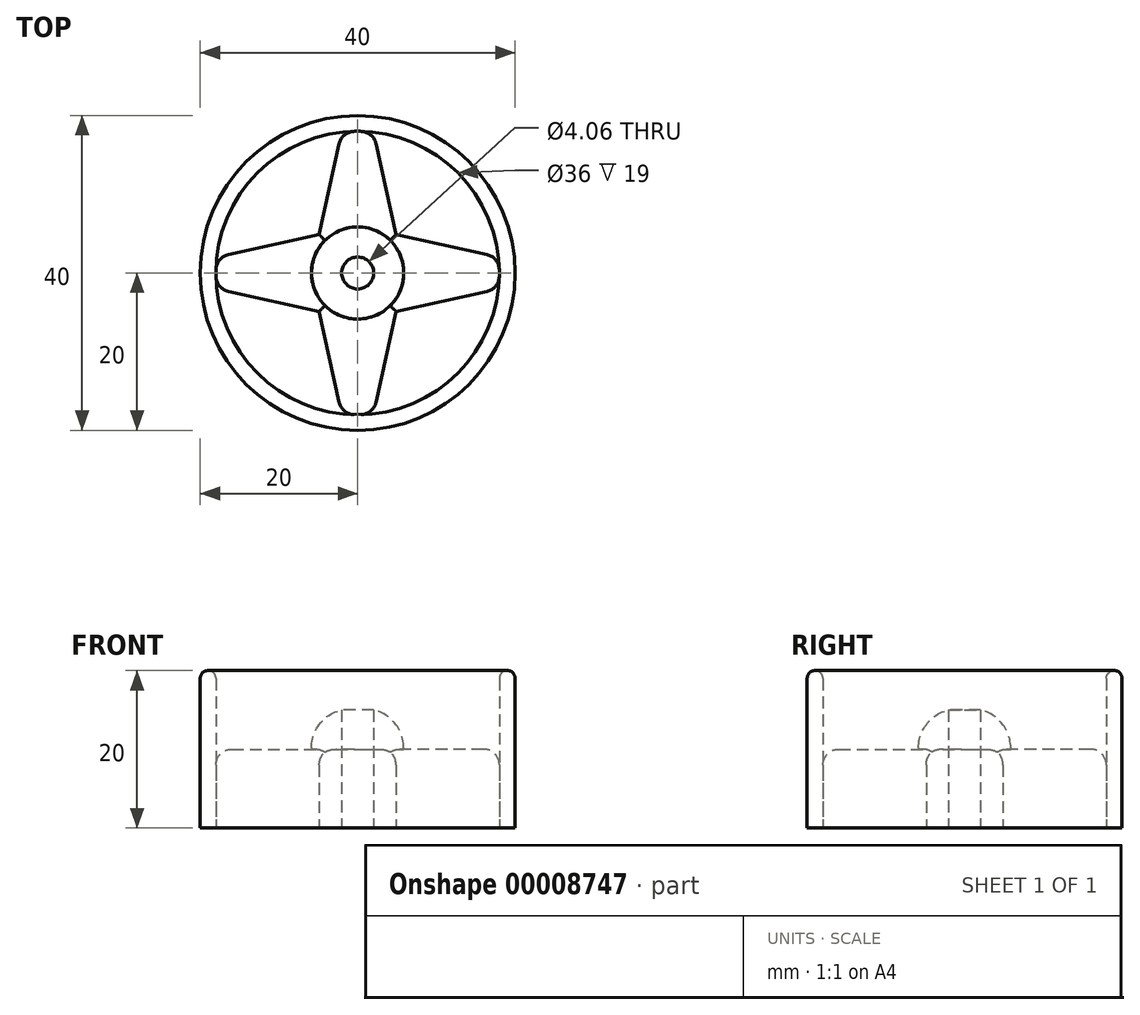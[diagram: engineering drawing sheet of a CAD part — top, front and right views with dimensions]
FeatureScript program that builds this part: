
annotation { "Feature Type Name" : "Feature", "Feature Type Description" : "" }
export const myFeature = defineFeature(function(context is Context, id is Id, definition is map)
    precondition{}
    {
        {
            var Q0;
            Q0=qCreatedBy(makeId("Top.planeOp"),FACE);
            var sketch = newSketch(context, id + "F0", { "sketchPlane" : qUnion([Q0])});
            skCircle(sketch, "E0", {"center": v(0, 0) * mm, "radius": 20 * mm});
            skCircle(sketch, "E1.0", {"center": v(0, 0) * mm, "radius": 18 * mm});
            skCircle(sketch, "E2", {"center": v(0, 0) * mm, "radius": 5.86 * mm});
            skCircle(sketch, "E3", {"center": v(0, 0) * mm, "radius": 2.03 * mm});
            skLineSegment(sketch, "E4", {"start": v(-2.03, 17.89) * mm, "end": v(-4.88, 4.88) * mm});
            skLineSegment(sketch, "E5", {"start": v(-17.89, 2.03) * mm, "end": v(-4.88, 4.88) * mm});
            skLineSegment(sketch, "E6.0.MirrorCS", {"start": v(-17.89, -2.03) * mm, "end": v(-4.88, -4.88) * mm});
            skLineSegment(sketch, "E7.0.MirrorCS", {"start": v(17.89, 2.03) * mm, "end": v(4.88, 4.88) * mm});
            skLineSegment(sketch, "E8.0.MirrorCS", {"start": v(17.89, -2.03) * mm, "end": v(4.88, -4.88) * mm});
            skLineSegment(sketch, "E9.0.MirrorCS", {"start": v(2.03, 17.89) * mm, "end": v(4.88, 4.88) * mm});
            skLineSegment(sketch, "E10.0.MirrorCS", {"start": v(-2.03, -17.89) * mm, "end": v(-4.88, -4.88) * mm});
            skLineSegment(sketch, "E11.0.MirrorCS", {"start": v(2.03, -17.89) * mm, "end": v(4.88, -4.88) * mm});
            skPoint(sketch, "E12.start.orphan", {"position": v(0, 18) * mm});
            skPoint(sketch, "E13.orphan", {"position": v(-2, 5.5) * mm});
            skPoint(sketch, "E14.orphan", {"position": v(-5.5, 2) * mm});
            skPoint(sketch, "E15.start.orphan", {"position": v(-5.86, 0) * mm});
            skSolve(sketch);
        }
        {
            var Q0;
            Q0=makeQuery(id+"F0.imprint","IMPRINT",FACE,{"disambiguationData":[TD([[makeQuery(id+"F0.imprint","IMPRINT",EDGE,{"derivedFrom":sQuery(id+"F0.wireOp",EDGE,"E0")}),1.0]])]});
            extrude(context, id + "F1", {"entities" : qUnion([Q0]), "depth" : 20 * mm});
        }
        {
            var Q0;
            Q0=makeQuery(id+"F0.imprint","IMPRINT",FACE,{"disambiguationData":[TD([[makeQuery(id+"F0.imprint","IMPRINT",EDGE,{"derivedFrom":sQuery(id+"F0.wireOp",EDGE,"E2")}),-1.0]])]});
            extrude(context, id + "F2", {"entities" : qUnion([Q0]), "depth" : 10 * mm});
        }
        {
            var Q0;
            Q0=makeQuery(id+"F0.imprint","IMPRINT",FACE,{"disambiguationData":[TD([[makeQuery(id+"F0.imprint","IMPRINT",EDGE,{"derivedFrom":sQuery(id+"F0.wireOp",EDGE,"E2")}),1.0]])]});
            extrude(context, id + "F3", {"entities" : qUnion([Q0]), "operationType" : NewBodyOperationType.ADD, "depth" : 15 * mm});
        }
        {
            var Q0;
            Q0=makeQuery(id+"F2.opExtrude","CAP_EDGE",EDGE,{"disambiguationData":[OSD([sQuery(id+"F0.wireOp",EDGE,"E4")])],"isStart":false});
            var Q1;
            Q1=makeQuery(id+"F2.opExtrude","CAP_EDGE",EDGE,{"disambiguationData":[OSD([sQuery(id+"F0.wireOp",EDGE,"E5")])],"isStart":false});
            var Q2;
            Q2=makeQuery(id+"F2.opExtrude","CAP_EDGE",EDGE,{"disambiguationData":[OSD([sQuery(id+"F0.wireOp",EDGE,"E6.0.MirrorCS")])],"isStart":false});
            var Q3;
            Q3=makeQuery(id+"F2.opExtrude","CAP_EDGE",EDGE,{"disambiguationData":[OSD([sQuery(id+"F0.wireOp",EDGE,"E10.0.MirrorCS")])],"isStart":false});
            var Q4;
            Q4=makeQuery(id+"F2.opExtrude","CAP_EDGE",EDGE,{"disambiguationData":[OSD([sQuery(id+"F0.wireOp",EDGE,"E11.0.MirrorCS")])],"isStart":false});
            var Q5;
            Q5=makeQuery(id+"F2.opExtrude","CAP_EDGE",EDGE,{"disambiguationData":[OSD([sQuery(id+"F0.wireOp",EDGE,"E8.0.MirrorCS")])],"isStart":false});
            var Q6;
            Q6=makeQuery(id+"F2.opExtrude","CAP_EDGE",EDGE,{"disambiguationData":[OSD([sQuery(id+"F0.wireOp",EDGE,"E7.0.MirrorCS")])],"isStart":false});
            var Q7;
            Q7=makeQuery(id+"F2.opExtrude","CAP_EDGE",EDGE,{"disambiguationData":[OSD([sQuery(id+"F0.wireOp",EDGE,"E9.0.MirrorCS")])],"isStart":false});
            fillet(context, id + "F4", {"entities" : qUnion([Q0, Q1, Q2, Q3, Q4, Q5, Q6, Q7]), "radius" : 2 * mm, "allowEdgeOverflow" : false});
        }
        {
            var Q0;
            Q0=makeQuery(id+"F3.opExtrude","CAP_EDGE",EDGE,{"disambiguationData":[OSD([sQuery(id+"F0.wireOp",EDGE,"E2")])],"isStart":false});
            fillet(context, id + "F5", {"entities" : qUnion([Q0]), "radius" : 5 * mm, "tangentPropagation" : true, "allowEdgeOverflow" : false});
        }
        {
            var Q0;
            Q0=makeQuery(id+"F1.opExtrude","CAP_FACE",FACE,{"disambiguationData":[OSD([sQuery(id+"F0.wireOp",EDGE,"E0"),sQuery(id+"F0.wireOp",EDGE,"E1.0"),sQuery(id+"F0.wireOp",EDGE,"aa337d1e-bd78-4951-a328-375c114ad06f.0"),sQuery(id+"F0.wireOp",EDGE,"7219519c-3e05-4d61-9cbf-932767d396e7.0"),sQuery(id+"F0.wireOp",EDGE,"E4"),sQuery(id+"F0.wireOp",EDGE,"E5")])],"isStart":false});
            fillet(context, id + "F6", {"entities" : qUnion([Q0]), "radius" : 1 * mm, "allowEdgeOverflow" : false});
        }
        {
            var Q0;
            Q0=makeQuery(id+"F4.opFillet","BLEND_EDGE",EDGE,{"blendedFrom":[makeQuery(id+"F2.opExtrude","CAP_EDGE",EDGE,{"disambiguationData":[OSD([sQuery(id+"F0.wireOp",EDGE,"E11.0.MirrorCS")])],"isStart":false}),makeQuery(id+"F1.opExtrude","SWEPT_FACE",FACE,{"disambiguationData":[OSD([sQuery(id+"F0.wireOp",EDGE,"E1.0")])]})],"blendedInto":[makeQuery(id+"F1.opExtrude","SWEPT_FACE",FACE,{"disambiguationData":[OSD([sQuery(id+"F0.wireOp",EDGE,"E1.0")])]})]});
            var Q1;
            Q1=makeQuery(id+"F4.opFillet","BLEND_EDGE",EDGE,{"blendedFrom":[makeQuery(id+"F2.opExtrude","CAP_EDGE",EDGE,{"disambiguationData":[OSD([sQuery(id+"F0.wireOp",EDGE,"E10.0.MirrorCS")])],"isStart":false}),makeQuery(id+"F1.opExtrude","SWEPT_FACE",FACE,{"disambiguationData":[OSD([sQuery(id+"F0.wireOp",EDGE,"E1.0")])]})],"blendedInto":[makeQuery(id+"F1.opExtrude","SWEPT_FACE",FACE,{"disambiguationData":[OSD([sQuery(id+"F0.wireOp",EDGE,"E1.0")])]})]});
            var Q2;
            Q2=makeQuery(id+"F2.opExtrude","SWEPT_EDGE",EDGE,{"disambiguationData":[OSD([sQuery(id+"F0.wireOp",EDGE,"E1.0"),sQuery(id+"F0.wireOp",EDGE,"E11.0.MirrorCS")])]});
            var Q3;
            Q3=makeQuery(id+"F2.opExtrude","SWEPT_EDGE",EDGE,{"disambiguationData":[OSD([sQuery(id+"F0.wireOp",EDGE,"E1.0"),sQuery(id+"F0.wireOp",EDGE,"E10.0.MirrorCS")])]});
            fillet(context, id + "F7", {"entities" : qUnion([Q0, Q1, Q2, Q3]), "radius" : 2 * mm, "tangentPropagation" : true, "allowEdgeOverflow" : false});
        }
        {
            var Q0;
            Q0=makeQuery(id+"F2.opExtrude","SWEPT_EDGE",EDGE,{"disambiguationData":[OSD([sQuery(id+"F0.wireOp",EDGE,"E1.0"),sQuery(id+"F0.wireOp",EDGE,"E8.0.MirrorCS")])]});
            var Q1;
            Q1=makeQuery(id+"F4.opFillet","BLEND_EDGE",EDGE,{"blendedFrom":[makeQuery(id+"F2.opExtrude","CAP_EDGE",EDGE,{"disambiguationData":[OSD([sQuery(id+"F0.wireOp",EDGE,"E8.0.MirrorCS")])],"isStart":false}),makeQuery(id+"F1.opExtrude","SWEPT_FACE",FACE,{"disambiguationData":[OSD([sQuery(id+"F0.wireOp",EDGE,"E1.0")])]})],"blendedInto":[makeQuery(id+"F1.opExtrude","SWEPT_FACE",FACE,{"disambiguationData":[OSD([sQuery(id+"F0.wireOp",EDGE,"E1.0")])]})]});
            var Q2;
            Q2=makeQuery(id+"F4.opFillet","BLEND_EDGE",EDGE,{"blendedFrom":[makeQuery(id+"F2.opExtrude","CAP_EDGE",EDGE,{"disambiguationData":[OSD([sQuery(id+"F0.wireOp",EDGE,"E7.0.MirrorCS")])],"isStart":false}),makeQuery(id+"F1.opExtrude","SWEPT_FACE",FACE,{"disambiguationData":[OSD([sQuery(id+"F0.wireOp",EDGE,"E1.0")])]})],"blendedInto":[makeQuery(id+"F1.opExtrude","SWEPT_FACE",FACE,{"disambiguationData":[OSD([sQuery(id+"F0.wireOp",EDGE,"E1.0")])]})]});
            var Q3;
            Q3=makeQuery(id+"F2.opExtrude","SWEPT_EDGE",EDGE,{"disambiguationData":[OSD([sQuery(id+"F0.wireOp",EDGE,"E1.0"),sQuery(id+"F0.wireOp",EDGE,"E7.0.MirrorCS")])]});
            var Q4;
            Q4=makeQuery(id+"F2.opExtrude","SWEPT_EDGE",EDGE,{"disambiguationData":[OSD([sQuery(id+"F0.wireOp",EDGE,"E1.0"),sQuery(id+"F0.wireOp",EDGE,"E6.0.MirrorCS")])]});
            var Q5;
            Q5=makeQuery(id+"F4.opFillet","BLEND_EDGE",EDGE,{"blendedFrom":[makeQuery(id+"F2.opExtrude","CAP_EDGE",EDGE,{"disambiguationData":[OSD([sQuery(id+"F0.wireOp",EDGE,"E6.0.MirrorCS")])],"isStart":false}),makeQuery(id+"F1.opExtrude","SWEPT_FACE",FACE,{"disambiguationData":[OSD([sQuery(id+"F0.wireOp",EDGE,"E1.0")])]})],"blendedInto":[makeQuery(id+"F1.opExtrude","SWEPT_FACE",FACE,{"disambiguationData":[OSD([sQuery(id+"F0.wireOp",EDGE,"E1.0")])]})]});
            var Q6;
            Q6=makeQuery(id+"F4.opFillet","BLEND_EDGE",EDGE,{"blendedFrom":[makeQuery(id+"F2.opExtrude","CAP_EDGE",EDGE,{"disambiguationData":[OSD([sQuery(id+"F0.wireOp",EDGE,"E5")])],"isStart":false}),makeQuery(id+"F1.opExtrude","SWEPT_FACE",FACE,{"disambiguationData":[OSD([sQuery(id+"F0.wireOp",EDGE,"E1.0")])]})],"blendedInto":[makeQuery(id+"F1.opExtrude","SWEPT_FACE",FACE,{"disambiguationData":[OSD([sQuery(id+"F0.wireOp",EDGE,"E1.0")])]})]});
            var Q7;
            Q7=makeQuery(id+"F2.opExtrude","SWEPT_EDGE",EDGE,{"disambiguationData":[OSD([sQuery(id+"F0.wireOp",EDGE,"E1.0"),sQuery(id+"F0.wireOp",EDGE,"E5")])]});
            var Q8;
            Q8=makeQuery(id+"F2.opExtrude","SWEPT_EDGE",EDGE,{"disambiguationData":[OSD([sQuery(id+"F0.wireOp",EDGE,"E1.0"),sQuery(id+"F0.wireOp",EDGE,"E4")])]});
            var Q9;
            Q9=makeQuery(id+"F4.opFillet","BLEND_EDGE",EDGE,{"blendedFrom":[makeQuery(id+"F2.opExtrude","CAP_EDGE",EDGE,{"disambiguationData":[OSD([sQuery(id+"F0.wireOp",EDGE,"E4")])],"isStart":false}),makeQuery(id+"F1.opExtrude","SWEPT_FACE",FACE,{"disambiguationData":[OSD([sQuery(id+"F0.wireOp",EDGE,"E1.0")])]})],"blendedInto":[makeQuery(id+"F1.opExtrude","SWEPT_FACE",FACE,{"disambiguationData":[OSD([sQuery(id+"F0.wireOp",EDGE,"E1.0")])]})]});
            var Q10;
            Q10=makeQuery(id+"F2.opExtrude","SWEPT_EDGE",EDGE,{"disambiguationData":[OSD([sQuery(id+"F0.wireOp",EDGE,"E1.0"),sQuery(id+"F0.wireOp",EDGE,"E9.0.MirrorCS")])]});
            var Q11;
            Q11=makeQuery(id+"F4.opFillet","BLEND_EDGE",EDGE,{"blendedFrom":[makeQuery(id+"F2.opExtrude","CAP_EDGE",EDGE,{"disambiguationData":[OSD([sQuery(id+"F0.wireOp",EDGE,"E9.0.MirrorCS")])],"isStart":false}),makeQuery(id+"F1.opExtrude","SWEPT_FACE",FACE,{"disambiguationData":[OSD([sQuery(id+"F0.wireOp",EDGE,"E1.0")])]})],"blendedInto":[makeQuery(id+"F1.opExtrude","SWEPT_FACE",FACE,{"disambiguationData":[OSD([sQuery(id+"F0.wireOp",EDGE,"E1.0")])]})]});
            fillet(context, id + "F8", {"entities" : qUnion([Q0, Q1, Q2, Q3, Q4, Q5, Q6, Q7, Q8, Q9, Q10, Q11]), "radius" : 2 * mm, "tangentPropagation" : true, "allowEdgeOverflow" : false});
        }
    });
